# Revit family: E-47
name_source: partatom
category: Plumbing Fixtures
revit_build: Autodesk Revit 2014 (Build: 20130308_1515(x64)
units: mm (PartAtom-declared; Revit-internal decimal feet)

## types (1)
- E-47
    Brass Chromed = Brass Chromed
    CW Connection = Yes
    Description = Nuva Shower and/or Tub Single Control With Diverter
    Documentation = http://www.helvex.com.mx
    Features = Ceramic Cartridge
    HW Connection = Yes
    Inlet Threads = 1/2" - 14 Npt Shower and 3/4" - 14 Npt Tub
    Manufacturer = Helvex
    Model = E-47
    Niquel Duravex = Niquel Duravex
    Satin = Satin
    Shower Valve Installation Depth Range = 12.7 mm (0.5") Max
    Total Height = 8"
    Total Length = 6"
    Total Width = 4"
    Type Comments = Single Control Faucets
    URL = http://www.helvex.com.mx
    Working Pressure = Pmin= 1.0 Kg/Cm² (14.22 Psi); Pmax= 6.00 Kg/Cm² (85.34 Psi)

## geometry (parser evidence)
native form markers: Sweep x3
no freeform markers — native parametric forms only
